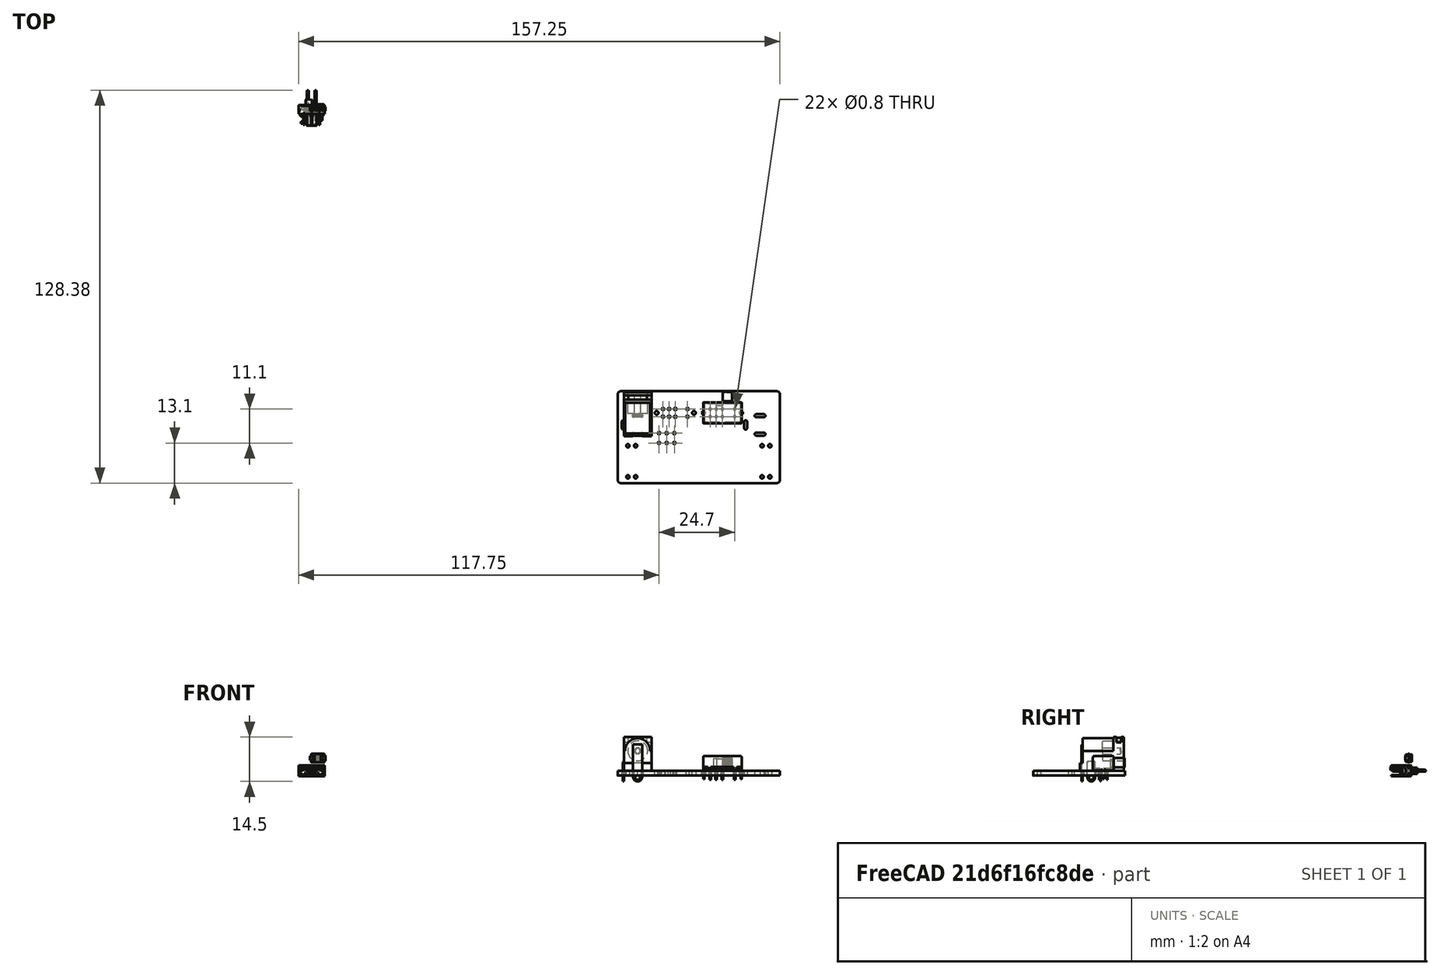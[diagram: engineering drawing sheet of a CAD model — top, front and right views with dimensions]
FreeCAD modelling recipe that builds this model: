
FCSTD DOCUMENT  (FreeCAD 1.0R39109 (Git))
Label: breadboard-power-supply
License: All rights reserved
LicenseURL: https://en.wikipedia.org/wiki/All_rights_reserved
objects: Part::Feature×27, App::Part×13, App::Link×11, PartDesign::CoordinateSystem×1, Sketcher::SketchObject×1
note: 30 computed .brp shape members not serialized (recipe doc carries the construction recipe); baked Part::Feature solids carry a one-line shape summary decoded from their .brp

FEATURE [PartDesign::CoordinateSystem] Local_CS_8d0f
  AttacherType = Attacher::AttachEngine3D
  MapMode = 2
FEATURE [Part::Feature] Pcb_8d0f
  shape: bbox 53 x 30 x 1.6 mm, 80 faces (baked)
FEATURE [Sketcher::SketchObject] PCB_Sketch_8d0f
  ArcFitTolerance = 1e-06
  FullyConstrained = false
  MakeInternals = false
  sketch-geometry (8):
    g0: LineSegment StartX=101 StartY=-90 StartZ=0 EndX=152 EndY=-90 EndZ=0
    g1: LineSegment StartX=152 StartY=-120 StartZ=0 EndX=101 EndY=-120 EndZ=0
    g2: LineSegment StartX=100 StartY=-119 StartZ=0 EndX=100 EndY=-91 EndZ=0
    g3: LineSegment StartX=153 StartY=-91 StartZ=0 EndX=153 EndY=-119 EndZ=0
    g4: ArcOfCircle CenterX=152 CenterY=-91 CenterZ=0 NormalX=0 NormalY=0 NormalZ=-1 AngleXU=1.5708 Radius=0.999999 StartAngle=0 EndAngle=1.5708
    g5: ArcOfCircle CenterX=101 CenterY=-119 CenterZ=0 NormalX=0 NormalY=0 NormalZ=-1 AngleXU=-1.5708 Radius=0.999999 StartAngle=0 EndAngle=1.5708
    g6: ArcOfCircle CenterX=101 CenterY=-91 CenterZ=0 NormalX=0 NormalY=0 NormalZ=-1 AngleXU=-7.47076e-07 Radius=0.999999 StartAngle=0 EndAngle=1.5708
    g7: ArcOfCircle CenterX=152 CenterY=-119 CenterZ=0 NormalX=0 NormalY=0 NormalZ=-1 AngleXU=3.14159 Radius=0.999999 StartAngle=0 EndAngle=1.5708
  constraints (8):
    c: Coincident(g2,g5)
    c: Coincident(g2,g6)
    c: Coincident(g1,g5)
    c: Coincident(g0,g6)
    c: Coincident(g1,g7)
    c: Coincident(g0,g4)
    c: Coincident(g3,g7)
    c: Coincident(g3,g4)
FEATURE [App::Part] Board_Geoms_8d0f
  Group = -> [Pcb_8d0f,PCB_Sketch_8d0f]
  Origin = -> Origin
FEATURE [Part::Feature] Part__Feature  label="LF 736"
  Placement = pos=(1.69926,2.64276,4.10843) rot=(0,0,1;0rad)
  shape: bbox 1.62 x 1.275 x 1.5 mm, 25 faces (baked)
FEATURE [Part::Feature] Part__Feature001  label="LF 737"
  Placement = pos=(1.69926,2.64276,4.10843) rot=(0,0,1;0rad)
  shape: bbox 3.12 x 1.275 x 1.78 mm, 27 faces (baked)
FEATURE [App::Part] LF_736  label="LF 738"
  Group = -> [Part__Feature,Part__Feature001]
  Origin = -> Origin008
FEATURE [Part::Feature] Part__Feature002  label="Die 35mil 270um"
  Placement = pos=(1.69926,2.97276,4.10843) rot=(1,0,0;1.5708rad)
  shape: bbox 0.89 x 0.3 x 0.89 mm, 6 faces (baked)
FEATURE [Part::Feature] Part__Feature003  label="Clip553 670"
  Placement = pos=(1.69926,3.15276,4.10843) rot=(0,0,1;0rad)
  shape: bbox 2.25 x 0.704 x 1.5 mm, 32 faces (baked)
FEATURE [Part::Feature] Part__Feature004  label="Áã¼þ2^B1100"
  Placement = pos=(1.69926,2.64276,4.10843) rot=(-1,0,0;1.5708rad)
  shape: bbox 0.91 x 0.03 x 0.91 mm, 6 faces (baked)
FEATURE [Part::Feature] Part__Feature005  label="Áã¼þ2^B1101"
  Placement = pos=(1.69926,2.64276,4.10843) rot=(-1,0,0;1.5708rad)
  shape: bbox 0.46 x 0.03 x 0.46 mm, 6 faces (baked)
FEATURE [Part::Feature] Part__Feature006  label="Áã¼þ2^B1102"
  Placement = pos=(1.69926,2.64276,4.10843) rot=(-1,0,0;1.5708rad)
  shape: bbox 0.3846 x 0.205 x 1.2 mm, 8 faces (baked)
FEATURE [App::Part] ________2_B1100  label="Áã¼þ2^B1103"
  Group = -> [Part__Feature004,Part__Feature005,Part__Feature006]
  Origin = -> Origin009
FEATURE [Part::Feature] Part__Feature007  label="SMA Compound 736 553 670"
  Placement = pos=(-0.14074,2.63876,2.70843) rot=(-1,0,0;1.5708rad)
  shape: bbox 4.301 x 2 x 2.8 mm, 146 faces (baked)
FEATURE [App::Part] new_SMA_20R  label="D2_new SMA 20R_0952939a186b"
  Group = -> [LF_736,Part__Feature002,Part__Feature003,________2_B1100,Part__Feature007]
  Origin = -> Origin010
  Placement = pos=(128.39,-107.8,-1.6) rot=(0.57735,0.57735,0.57735;2.0944rad)
FEATURE [Part::Feature] Part__Feature008  label="EG1271--3DModel-STEP-520916"
  Placement = pos=(-0.95,3.3,1e-16) rot=(-1,0,0;1.5708rad)
  shape: bbox 8.5 x 8.5 x 3.6 mm, 203 faces (baked)
FEATURE [App::Part] EG1271  label="SW1_EG1271_2816c8904585"
  Group = -> [Part__Feature008]
  Origin = -> Origin011
  Placement = pos=(116,-105.3,0) rot=(1,0,0;1.5708rad)
FEATURE [Part::Feature] Part__Feature009  label="C0805C104K5RACTU"
  shape: bbox 2.3 x 0.98 x 1.55 mm, 58 faces (baked)
FEATURE [Part::Feature] Part__Feature010  label="C0805C104K5RACTU001"
  shape: bbox 0.2279 x 0.005 x 0.4313 mm, 19 faces (baked)
FEATURE [Part::Feature] Part__Feature011  label="C0805C104K5RACTU002"
  shape: bbox 0.2279 x 0.005 x 0.5256 mm, 25 faces (baked)
FEATURE [Part::Feature] Part__Feature012  label="C0805C104K5RACTU003"
  shape: bbox 0.2279 x 0.005 x 0.2743 mm, 13 faces (baked)
FEATURE [App::Part] C0805C104K5RACTU  label="C1_C0805C104K5RACTU004_20f41c0f8bfd"
  Group = -> [Part__Feature009,Part__Feature010,Part__Feature011,Part__Feature012]
  Origin = -> Origin012
  Placement = pos=(120.9,-103.75,0) rot=(0.57735,-0.57735,-0.57735;2.0944rad)
FEATURE [App::Link] D2_new_SMA_20R_0952939a186b_ln_  label="D1_new SMA 20R_7dfb9a78bb62"
  LinkPlacement = pos=(122.5,-108.69,-1.6) rot=(1,0,0;1.5708rad)
  LinkedObject = -> new_SMA_20R
  Placement = pos=(122.5,-108.69,-1.6) rot=(1,0,0;1.5708rad)
FEATURE [Part::Feature] Shape  label="SW3_EG2315_80b6656eb97f"
  Placement = pos=(134.2,-97.05,-3) rot=(0,0,1;3.14159rad)
  shape: bbox 12.6 x 10.3 x 7.8 mm, 150 faces (baked)
FEATURE [Part::Feature] Part__Feature013  label="RCS0805120RFKEA"
  shape: bbox 1.95 x 0.45 x 1.25 mm, 6 faces (baked)
FEATURE [Part::Feature] Part__Feature014  label="RCS0805120RFKEA001"
  shape: bbox 1.4 x 0.025 x 1.25 mm, 6 faces (baked)
FEATURE [Part::Feature] Part__Feature015  label="RCS0805120RFKEA002"
  shape: bbox 0.3 x 0.5 x 1.25 mm, 14 faces (baked)
FEATURE [Part::Feature] Part__Feature016  label="RCS0805120RFKEA003"
  shape: bbox 0.3 x 0.5 x 1.25 mm, 14 faces (baked)
FEATURE [App::Part] RCS0805120RFKEA  label="R2_RCS0805120RFKEA004_a3deb157f018"
  Group = -> [Part__Feature013,Part__Feature014,Part__Feature015,Part__Feature016]
  Origin = -> Origin013
  Placement = pos=(113.87,-101.6,0) rot=(0,0.707107,0.707107;3.14159rad)
FEATURE [App::Link] C1_C0805C104K5RACTU004_20f41c0f8bfd_ln_  label="C3_C0805C104K5RACTU004_ad2479d6b090"
  LinkPlacement = pos=(136.3,-104.05,0) rot=(0.57735,0.57735,0.57735;2.0944rad)
  LinkedObject = -> C0805C104K5RACTU
  Placement = pos=(136.3,-104.05,0) rot=(0.57735,0.57735,0.57735;2.0944rad)
FEATURE [App::Link] R2_RCS0805120RFKEA004_a3deb157f018_ln_  label="R1_RCS0805120RFKEA004_754ceaad8c13"
  LinkPlacement = pos=(135.5,-107.45,0) rot=(0.57735,0.57735,0.57735;2.0944rad)
  LinkedObject = -> RCS0805120RFKEA
  Placement = pos=(135.5,-107.45,0) rot=(0.57735,0.57735,0.57735;2.0944rad)
FEATURE [Part::Feature] Shape001  label="J1_CUI_DEVICES_PJ-002A_55e8efef0c78"
  Placement = pos=(106.5,-90.3,6.5) rot=(0.57735,0.57735,0.57735;2.0944rad)
  shape: bbox 9.4 x 14.4 x 14.5 mm, 57 faces (baked)
FEATURE [App::Link] SW3_EG2315_80b6656eb97f_ln_  label="SW2_EG2315_f7c61ab64d1e"
  LinkPlacement = pos=(118.8,-97.05,-3) rot=(0,0,1;3.14159rad)
  LinkedObject = -> Shape
  Placement = pos=(118.8,-97.05,-3) rot=(0,0,1;3.14159rad)
FEATURE [Part::Feature] Part__Feature017  label="BODY-SOT"
  Placement = pos=(0,0,0.7874) rot=(0.57735,-0.57735,-0.57735;2.0944rad)
  shape: bbox 3.5 x 6.5 x 1.6 mm, 14 faces (baked)
FEATURE [Part::Feature] Part__Feature018  label="LEAD-SOT"
  Placement = pos=(-2.7498,-2.2438,0.25) rot=(0.57735,-0.57735,-0.57735;2.0944rad)
  shape: bbox 1.75 x 0.75 x 0.7874 mm, 14 faces (baked)
FEATURE [Part::Feature] Part__Feature019  label="LEAD-SOT001"
  Placement = pos=(-2.7498,0.0562,0.25) rot=(0.57735,-0.57735,-0.57735;2.0944rad)
  shape: bbox 1.75 x 0.75 x 0.7874 mm, 14 faces (baked)
FEATURE [Part::Feature] Part__Feature020  label="LEAD-SOT002"
  Placement = pos=(-2.7498,2.3562,0.25) rot=(0.57735,-0.57735,-0.57735;2.0944rad)
  shape: bbox 1.75 x 0.75 x 0.7874 mm, 14 faces (baked)
FEATURE [Part::Feature] Part__Feature021  label="LEAD-SOT-WIDE"
  Placement = pos=(2.7498,0.0026,0.25) rot=(0.57735,0.57735,0.57735;2.0944rad)
  shape: bbox 1.75 x 3 x 0.7874 mm, 14 faces (baked)
FEATURE [App::Part] DCY0004A_ASM  label="U1_DCY0004A_ASM_2dbe2f4dbc05"
  Group = -> [Part__Feature017,Part__Feature018,Part__Feature019,Part__Feature020,Part__Feature021]
  Origin = -> Origin014
  Placement = pos=(126.5,-105.8,0) rot=(0,0,-1;1.5708rad)
FEATURE [App::Link] R2_RCS0805120RFKEA004_a3deb157f018_ln_001  label="R3_RCS0805120RFKEA004_74bbc2b843f3"
  LinkPlacement = pos=(117.73,-101.6,0) rot=(1,0,0;1.5708rad)
  LinkedObject = -> RCS0805120RFKEA
  Placement = pos=(117.73,-101.6,0) rot=(1,0,0;1.5708rad)
FEATURE [App::Link] J1_CUI_DEVICES_PJ_002A_55e8efef0c78_ln_  label="J2_CUI_DEVICES_PJ-002A_d9c951ac5020"
  LinkPlacement = pos=(146.5,-90.3,6.5) rot=(0.57735,0.57735,0.57735;2.0944rad)
  LinkedObject = -> Shape001
  Placement = pos=(146.5,-90.3,6.5) rot=(0.57735,0.57735,0.57735;2.0944rad)
FEATURE [App::Link] C1_C0805C104K5RACTU004_20f41c0f8bfd_ln_001  label="C2_C0805C104K5RACTU004_f27700a97261"
  LinkPlacement = pos=(131.65,-110.7,0) rot=(0,0.707107,0.707107;3.14159rad)
  LinkedObject = -> C0805C104K5RACTU
  Placement = pos=(131.65,-110.7,0) rot=(0,0.707107,0.707107;3.14159rad)
FEATURE [App::Link] D2_new_SMA_20R_0952939a186b_ln_001  label="D3_new SMA 20R_0e3b2a965611"
  LinkPlacement = pos=(122.5,-112.69,-1.6) rot=(1,0,0;1.5708rad)
  LinkedObject = -> new_SMA_20R
  Placement = pos=(122.5,-112.69,-1.6) rot=(1,0,0;1.5708rad)
FEATURE [App::Part] Top_8d0f
  Group = -> [new_SMA_20R,EG1271,C0805C104K5RACTU,D2_new_SMA_20R_0952939a186b_ln_,Shape,RCS0805120RFKEA,C1_C0805C104K5RACTU004_20f41c0f8bfd_ln_,R2_RCS0805120RFKEA004_a3deb157f018_ln_,Shape001,SW3_EG2315_80b6656eb97f_ln_,DCY0004A_ASM,R2_RCS0805120RFKEA004_a3deb157f018_ln_001,J1_CUI_DEVICES_PJ_002A_55e8efef0c78_ln_,C1_C0805C104K5RACTU004_20f41c0f8bfd_ln_001,D2_new_SMA_20R_0952939a186b_ln_001]
  Origin = -> Origin003
FEATURE [Part::Feature] Part__Feature022  label="TSW-102-07-F-S_body"
  shape: bbox 5.207 x 2.54 x 2.54 mm, 69 faces (baked)
FEATURE [Part::Feature] Part__Feature023  label="T-1S6-07-TSW-1-07-2-S"
  Placement = pos=(0,-2.54,0) rot=(0,0,1;0rad)
  shape: bbox 3.429 x 10.92 x 0.889 mm, 38 faces (baked)
FEATURE [App::Part] TSW_102_07_F_S  label="J6_TSW-102-07-F-S_af2df57303ab"
  Group = -> [Part__Feature022,Part__Feature023]
  Origin = -> Origin015
  Placement = pos=(148.43,-117.97,-1.6) rot=(-1,0,0;1.5708rad)
FEATURE [App::Link] J6_TSW_102_07_F_S_af2df57303ab_ln_  label="J3_TSW-102-07-F-S_91d19b5af423"
  LinkPlacement = pos=(104.57,-107.81,-1.6) rot=(0,0.707107,-0.707107;3.14159rad)
  LinkedObject = -> TSW_102_07_F_S
  Placement = pos=(104.57,-107.81,-1.6) rot=(0,0.707107,-0.707107;3.14159rad)
FEATURE [App::Link] J6_TSW_102_07_F_S_af2df57303ab_ln_001  label="J4_TSW-102-07-F-S_3f57c38ca013"
  LinkPlacement = pos=(104.57,-117.97,-1.6) rot=(-1,0,0;1.5708rad)
  LinkedObject = -> TSW_102_07_F_S
  Placement = pos=(104.57,-117.97,-1.6) rot=(-1,0,0;1.5708rad)
FEATURE [App::Link] J6_TSW_102_07_F_S_af2df57303ab_ln_002  label="J5_TSW-102-07-F-S_f7e907fcc812"
  LinkPlacement = pos=(148.43,-107.81,-1.6) rot=(0,0.707107,-0.707107;3.14159rad)
  LinkedObject = -> TSW_102_07_F_S
  Placement = pos=(148.43,-107.81,-1.6) rot=(0,0.707107,-0.707107;3.14159rad)
FEATURE [App::Part] Bot_8d0f
  Group = -> [TSW_102_07_F_S,J6_TSW_102_07_F_S_af2df57303ab_ln_,J6_TSW_102_07_F_S_af2df57303ab_ln_001,J6_TSW_102_07_F_S_af2df57303ab_ln_002]
  Origin = -> Origin004
FEATURE [App::Part] Step_Models_8d0f
  Group = -> [Top_8d0f,Bot_8d0f]
  Origin = -> Origin002
FEATURE [App::Part] Board_8d0f  label="breadboard-power-supply"
  Group = -> [Local_CS_8d0f,Board_Geoms_8d0f,Step_Models_8d0f]
  Origin = -> Origin001
